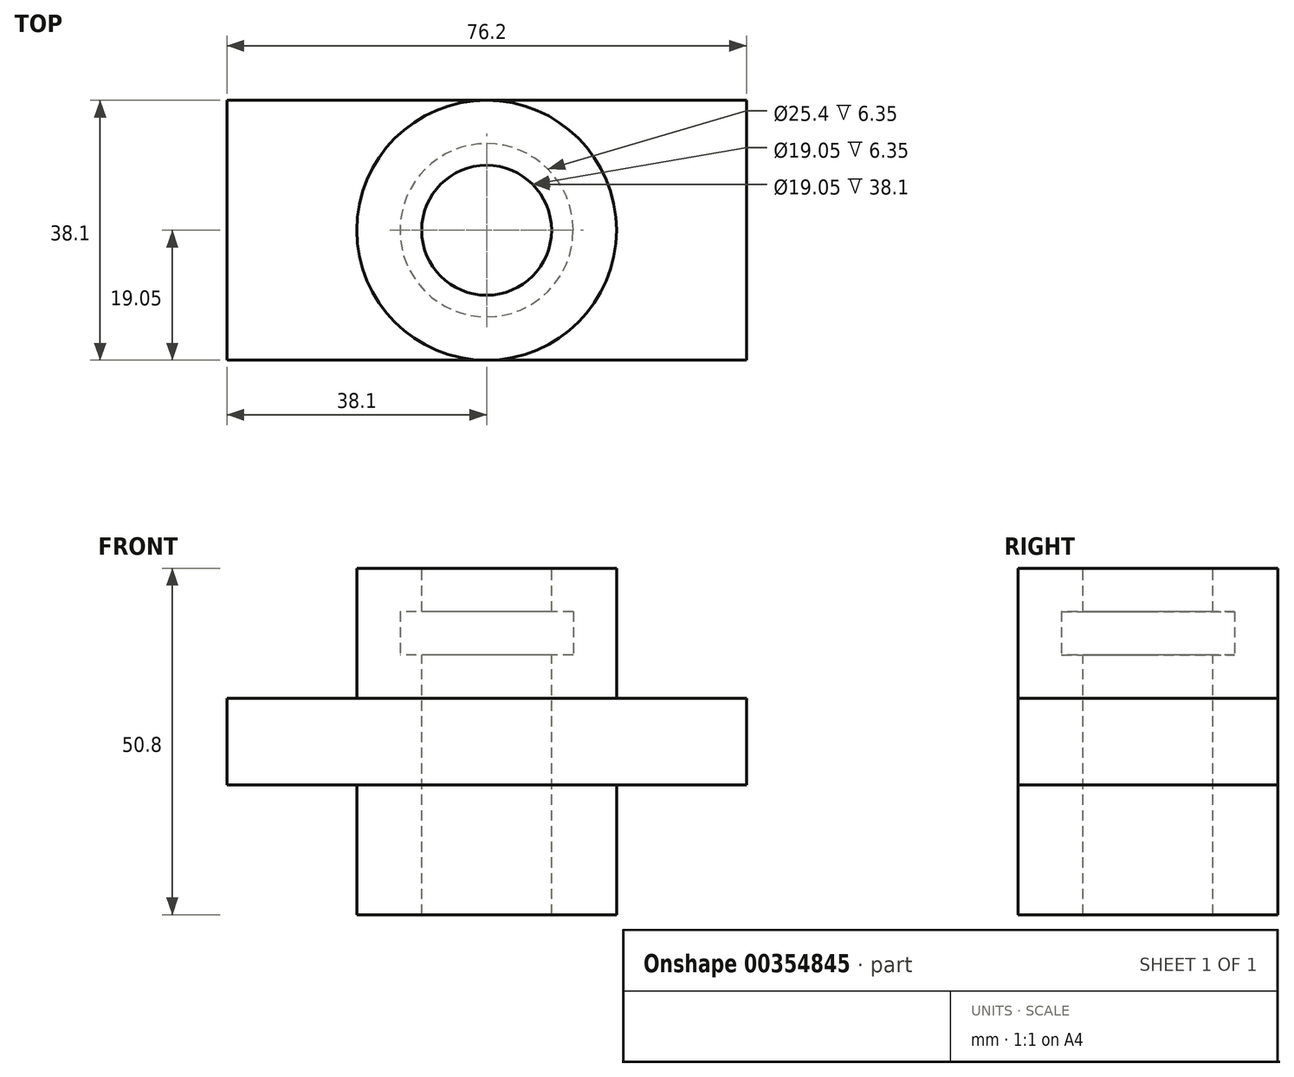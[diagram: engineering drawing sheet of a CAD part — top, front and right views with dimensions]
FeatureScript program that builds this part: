
annotation { "Feature Type Name" : "Feature", "Feature Type Description" : "" }
export const myFeature = defineFeature(function(context is Context, id is Id, definition is map)
    precondition{}
    {
        {
            var Q0;
            Q0=qCreatedBy(makeId("Top.planeOp"),FACE);
            var sketch = newSketch(context, id + "F0", { "sketchPlane" : qUnion([Q0])});
            skCircle(sketch, "E0", {"center": v(0, 0) * mm, "radius": 19.05 * mm});
            skSolve(sketch);
        }
        {
            var Q0;
            Q0 = qSketchRegion(id + "F0", true);
            extrude(context, id + "F1", {"entities" : qUnion([Q0]), "oppositeDirection" : true, "depth" : 25.4 * mm, "hasSecondDirection" : true, "secondDirectionOppositeDirection" : false, "secondDirectionDepth" : 12.7 * mm});
        }
        {
            var Q0;
            Q0=makeQuery(id+"F1.opExtrude","CAP_FACE",FACE,{"disambiguationData":[OSD([sQuery(id+"F0.wireOp",EDGE,"E0")])],"isStart":true});
            var sketch = newSketch(context, id + "F2", { "sketchPlane" : qUnion([Q0])});
            skCircle(sketch, "E1", {"center": v(0, 0) * mm, "radius": 12.7 * mm});
            skCircle(sketch, "E2.0.0", {"center": v(0, 0) * mm, "radius": 19.05 * mm});
            skSolve(sketch);
        }
        {
            var Q0;
            Q0 = qSketchRegion(id + "F2", true);
            extrude(context, id + "F3", {"entities" : qUnion([Q0]), "operationType" : NewBodyOperationType.ADD, "depth" : 6.35 * mm});
        }
        {
            var Q0;
            Q0=makeQuery(id+"F3.opExtrude","CAP_FACE",FACE,{"disambiguationData":[OSD([sQuery(id+"F2.wireOp",EDGE,"E1"),sQuery(id+"F2.wireOp",EDGE,"E2.0.0")])],"isStart":false});
            var sketch = newSketch(context, id + "F4", { "sketchPlane" : qUnion([Q0])});
            skCircle(sketch, "E3", {"center": v(0, 0) * mm, "radius": 19.05 * mm});
            skSolve(sketch);
        }
        {
            var Q0;
            Q0 = qSketchRegion(id + "F4", true);
            extrude(context, id + "F5", {"entities" : qUnion([Q0]), "operationType" : NewBodyOperationType.ADD, "depth" : 6.35 * mm});
        }
        {
            var Q0;
            Q0=makeQuery(id+"F5.opExtrude","CAP_FACE",FACE,{"disambiguationData":[OSD([sQuery(id+"F4.wireOp",EDGE,"E3")])],"isStart":false});
            var sketch = newSketch(context, id + "F6", { "sketchPlane" : qUnion([Q0])});
            skCircle(sketch, "E4", {"center": v(0, 0) * mm, "radius": 9.53 * mm});
            skSolve(sketch);
        }
        {
            var Q0;
            Q0 = qSketchRegion(id + "F6", true);
            extrude(context, id + "F7", {"entities" : qUnion([Q0]), "operationType" : NewBodyOperationType.REMOVE, "endBound" : BoundingType.THROUGH_ALL, "oppositeDirection" : true, "depth" : 25.4 * mm});
        }
        {
            var Q0;
            Q0=qCreatedBy(makeId("Top.planeOp"),FACE);
            var sketch = newSketch(context, id + "F8", { "sketchPlane" : qUnion([Q0])});
            skLineSegment(sketch, "E5.bottom", {"start": v(-38.1, 19.05) * mm, "end": v(38.1, 19.05) * mm});
            skLineSegment(sketch, "E5.top", {"start": v(-38.1, -19.05) * mm, "end": v(38.1, -19.05) * mm});
            skLineSegment(sketch, "E5.left", {"start": v(-38.1, 19.05) * mm, "end": v(-38.1, -19.05) * mm});
            skLineSegment(sketch, "E5.right", {"start": v(38.1, 19.05) * mm, "end": v(38.1, -19.05) * mm});
            skLineSegment(sketch, "E6", {"start": v(0, 30.82) * mm, "end": v(0, -34.56) * mm, "construction": true});
            skCircle(sketch, "E7.0.0", {"center": v(0, 0) * mm, "radius": 19.05 * mm});
            skSolve(sketch);
        }
        {
            var Q0;
            {var subQ0=sQuery(id+"F8.wireOp",EDGE,"E5.left");Q0=makeQuery(id+"F8.imprint","IMPRINT",FACE,{"disambiguationData":[TD([[makeQuery(id+"F8.imprint","IMPRINT",EDGE,{"derivedFrom":subQ0}),1.0]])]});}
            var Q1;
            {var subQ0=sQuery(id+"F8.wireOp",EDGE,"E5.right");Q1=makeQuery(id+"F8.imprint","IMPRINT",FACE,{"disambiguationData":[TD([[makeQuery(id+"F8.imprint","IMPRINT",EDGE,{"derivedFrom":subQ0}),-1.0]])]});}
            extrude(context, id + "F9", {"entities" : qUnion([Q0, Q1]), "operationType" : NewBodyOperationType.ADD, "endBound" : BoundingType.SYMMETRIC, "depth" : 12.7 * mm});
        }
    });
